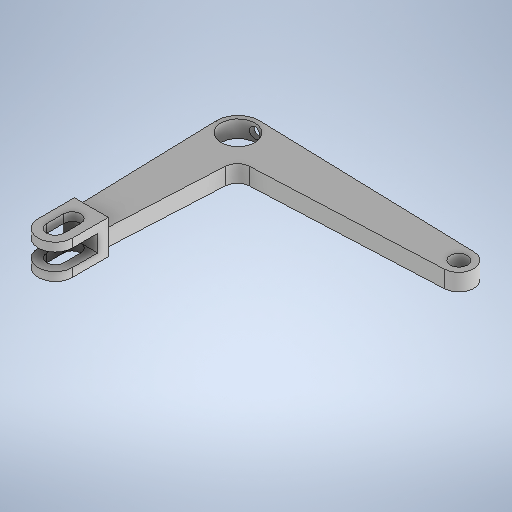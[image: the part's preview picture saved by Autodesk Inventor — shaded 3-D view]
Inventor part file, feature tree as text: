
AUTODESK INVENTOR PART (.ipt)
format: ipt  version: 2025.1 (Build 291241000, 241)  size: 349,184 bytes
history: native  units: mm
features: sketch x8, extrude x4, hole x3, fillet x1, plane x1, projected_geometry x1
ambient origin geometry x8: Origin, YZ Plane, XZ Plane, XY Plane, X Axis, Y Axis, Z Axis, Center Point
bodies: Solid1 (feature_tree)
feature tree (18):
  extrude  "Extrusion1"  Depth=8.0mm
  fillet  "Fillet1"  Radius=8.0mm
  extrude  "Extrusion3"  Depth=4.0mm
  extrude  "Extrusion4"  Depth=10.0mm TaperAngle=0.0deg
  plane  "Work Plane1"
  extrude  "Extrusion5"  Depth=10.0mm
  hole  "Hole1"  [1 undecoded]
  hole  "Hole2"  [1 undecoded]
  hole  "Hole3"  [1 undecoded]
  sketch  "Sketch10"  dims[d31=3.0mm d32=3.5mm d33=4.0mm d34=0.0mm d35=4.0mm d36=6.0mm d37=8.0mm d38=2.0mm d39=90.0deg d40=8.0mm d41=0.0mm d42=8.0mm d43=6.0mm d44=4.0mm d45=2.0mm d46=90.0deg d47=8.0mm d48=0.0mm d50=2.5mm d51=6.0mm d52=4.0mm d53=2.0mm d54=90.0deg d55=12.0mm d56=0.0mm d57=4.0mm d59=3.908mm]
  sketch  "Sketch2"  dims[d8=12.5mm d9=8.0mm d10=8.0mm d11=0.0mm]
  sketch  "Sketch4"  dims[d16=4.0mm d17=4.0mm]
  sketch  "Sketch5"  dims[d18=2.0mm d19=10.0mm d20=0.0mm]
  projected_geometry  "Projected Loop1"
  sketch  "Sketch6"  dims[d22=4.0mm d23=10.0mm]
  sketch  "Sketch7"  dims[d24=2.0mm d25=10.0mm d26=0.0mm]
  sketch  "Sketch8"  dims[d27=0.0mm d28=5.0mm]
  sketch  "Sketch9"  dims[d29=39.0mm d30=52.0mm]
note: 3 required parameter values undecoded (feature->parameter linkage not recoverable at this tier; creation-order binding heuristic only, values carry confidence <= 0.55)
